# Revit family: Konsole 45- 45 SP Platte quer
name_source: partatom
category: HLS-Bauteile
revit_build: Autodesk Revit 2017 (Build: 20190508_0315(x64)
units: mm (PartAtom-declared; Revit-internal decimal feet)

## family parameters
Basisbauteil = Fläche
Beim Laden mit Abzugskörper schneiden = Nein
Bemaßung runder Anschluss = Durchmesser verwenden
Gemeinsam genutzt = Ja
Raumberechnungspunkt = Nein
Teiletyp = Normal

## types (4) — shared parameters
Ausrichtung Platte = quer
Breite Platte = 50 mm  [stored 0.164042 ft]
Breite Profil = 45 mm  [stored 0.147638 ft]
Fabrikat = MEFA
Firma = MEFA Befestigungs- und Montagesysteme GmbH
Höhe Profil = 45 mm  [stored 0.147638 ft]
Kurztext1 = Konsole C-Profil 45/45
Langloch Platte = 14x20 mm
Lochabstand = 85 mm
Lochdurchmesser = 14 mm
Länge Platte = 127 mm
Material = Stahl
Materialname C-Profil = S235JR
Materialname Platte = S355J2
Oberflaeche = galvanisch verzinkt
Profil = C-Profil
Stärke Platte = 6 mm  [stored 0.019685 ft]
Stärke Profil = 3 mm  [stored 0.00984252 ft]
Vorgabe-Ansicht = 1219 mm

## per-type parameters (varying)
| type | Artikelnummer | EAN | Gewicht | Gewicht pro Bauteil | Kurztext2 | Länge Konsole | Schienenlänge | max. zul. Last F1 | max. zul. Last F2 | max. zul. Last q0 |
| Konsole 45- 45 SP L= 525 Platte quer gvz | 9992221 | 4250928449733 | 1.92 kg | 1.92 kg | L= 525 mm Platte quer gvz | 525 mm | Montageschiene 45- 45-2,5 für Konsole : C-Profil 45- 45-2,5 L=  525 | 0.33 kip | 0.17 kip | 0.192 kip/ft |
| Konsole 45- 45 SP L= 420 Platte quer gvz | 9992220 | 4250928448927 | 1.61 kg | 1.61 kg | L= 420 mm Platte quer gvz | 420 mm  [stored 1.37795 ft] | Montageschiene 45- 45-2,5 für Konsole : C-Profil 45- 45-2,5 L=  420 | 0.53 kip | 0.27 kip | 0.386 kip/ft |
| Konsole 45- 45 SP L= 315 Platte quer gvz | 9992219 | 4250928448910 | 1.30 kg | 1.30 kg | L= 315 mm Platte quer gvz | 315 mm  [stored 1.03346 ft] | Montageschiene 45- 45-2,5 für Konsole : C-Profil 45- 45-2,5 L=  315 | 0.71 kip | 0.36 kip | 0.686 kip/ft |
| Konsole 45- 45 SP L= 210 Platte quer gvz | 9992218 | 4250928449726 | 0.99 kg | 0.99 kg | L= 210 mm Platte quer gvz | 210 mm  [stored 0.688976 ft] | Montageschiene 45- 45-2,5 für Konsole : C-Profil 45- 45-2,5 L=  210 | 0.83 kip | 0.41 kip | 1.201 kip/ft |

note: [stored X ft] marks values corroborated as IEEE doubles in the binary element streams (Revit-internal decimal feet)
